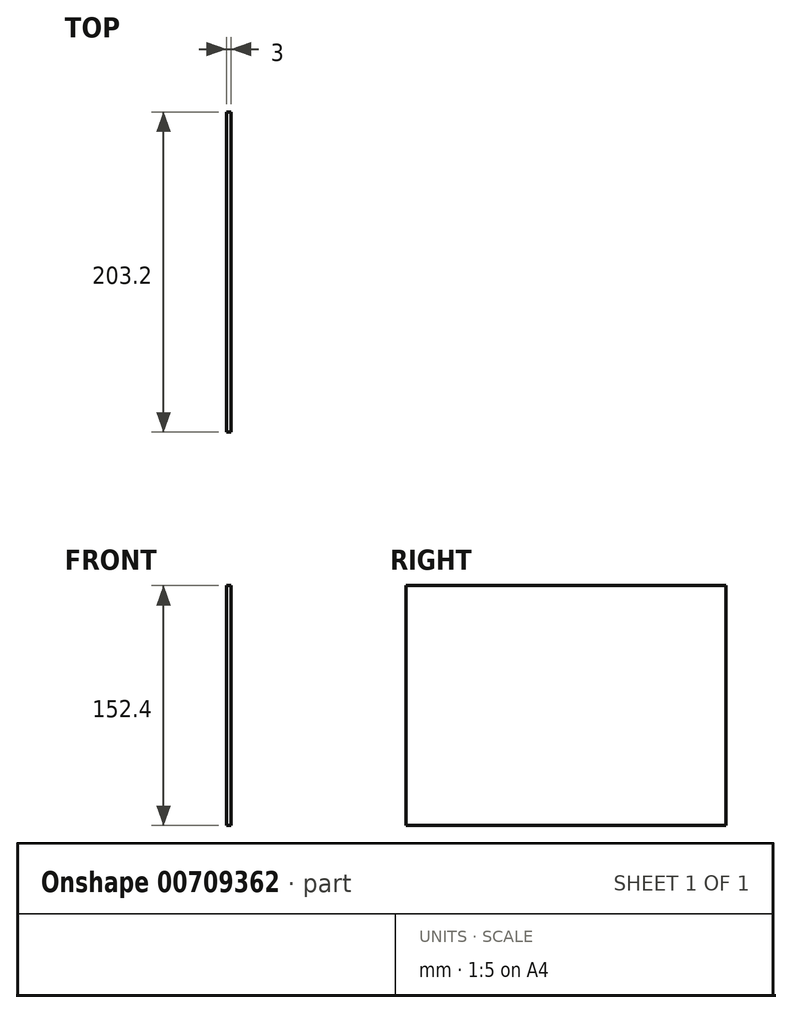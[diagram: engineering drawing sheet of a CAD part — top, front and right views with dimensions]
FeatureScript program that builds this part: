
annotation { "Feature Type Name" : "Feature", "Feature Type Description" : "" }
export const myFeature = defineFeature(function(context is Context, id is Id, definition is map)
    precondition{}
    {
        {
            var Q0;
            Q0=qCreatedBy(makeId("Right.planeOp"),FACE);
            var sketch = newSketch(context, id + "F0", { "sketchPlane" : qUnion([Q0])});
            skLineSegment(sketch, "E0.bottom", {"start": v(-56.3, 93.51) * mm, "end": v(146.9, 93.51) * mm});
            skLineSegment(sketch, "E0.top", {"start": v(-56.3, -58.89) * mm, "end": v(146.9, -58.89) * mm});
            skLineSegment(sketch, "E0.left", {"start": v(-56.3, 93.51) * mm, "end": v(-56.3, -58.89) * mm});
            skLineSegment(sketch, "E0.right", {"start": v(146.9, 93.51) * mm, "end": v(146.9, -58.89) * mm});
            skSolve(sketch);
        }
        {
            var Q0;
            Q0 = qSketchRegion(id + "F0", true);
            extrude(context, id + "F1", {"entities" : qUnion([Q0]), "depth" : 3 * mm, "offsetDistance" : 25.4 * mm});
        }
    });
